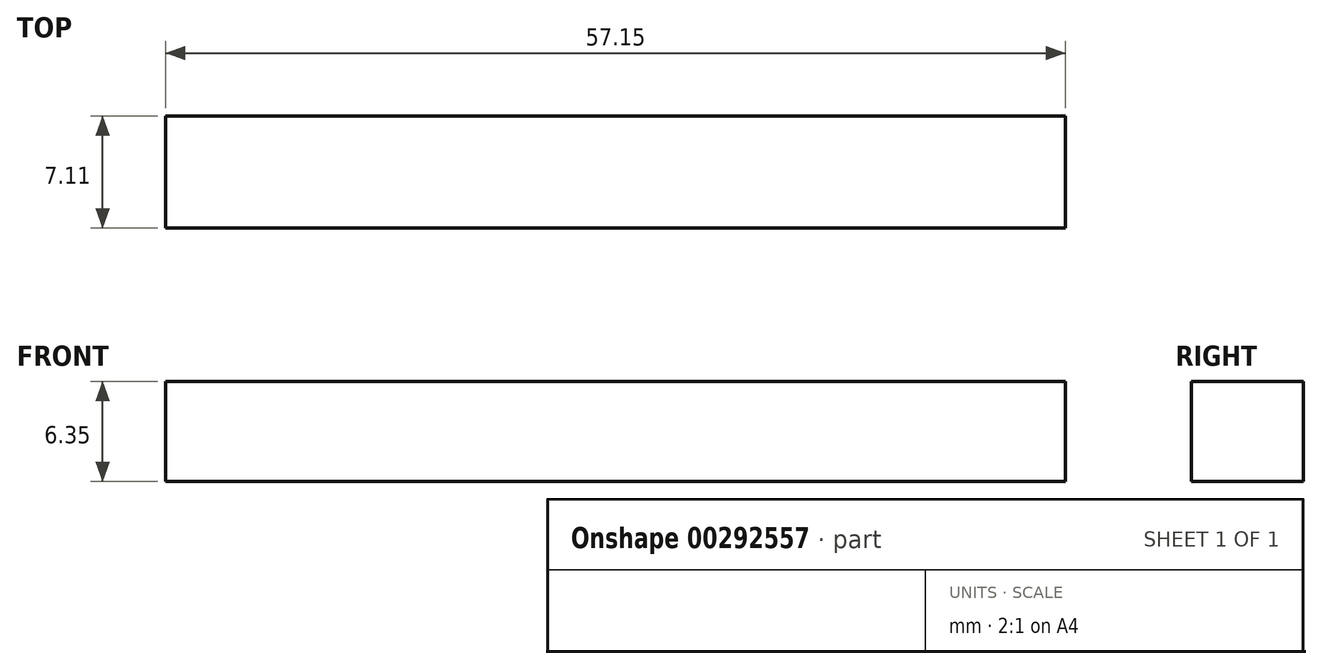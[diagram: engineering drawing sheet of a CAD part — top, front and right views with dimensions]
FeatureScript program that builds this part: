
annotation { "Feature Type Name" : "Feature", "Feature Type Description" : "" }
export const myFeature = defineFeature(function(context is Context, id is Id, definition is map)
    precondition{}
    {
        {
            var Q0;
            Q0=qCreatedBy(makeId("Front.planeOp"),FACE);
            var sketch = newSketch(context, id + "F0", { "sketchPlane" : qUnion([Q0])});
            skLineSegment(sketch, "E0.bottom", {"start": v(-5.94, 6.41) * mm, "end": v(51.21, 6.41) * mm});
            skLineSegment(sketch, "E0.top", {"start": v(-5.94, 0.06) * mm, "end": v(51.21, 0.06) * mm});
            skLineSegment(sketch, "E0.left", {"start": v(-5.94, 6.41) * mm, "end": v(-5.94, 0.06) * mm});
            skLineSegment(sketch, "E0.right", {"start": v(51.21, 6.41) * mm, "end": v(51.21, 0.06) * mm});
            skSolve(sketch);
        }
        {
            var Q0;
            Q0 = qSketchRegion(id + "F0", true);
            extrude(context, id + "F1", {"entities" : qUnion([Q0]), "depth" : 7.11 * mm});
        }
    });
